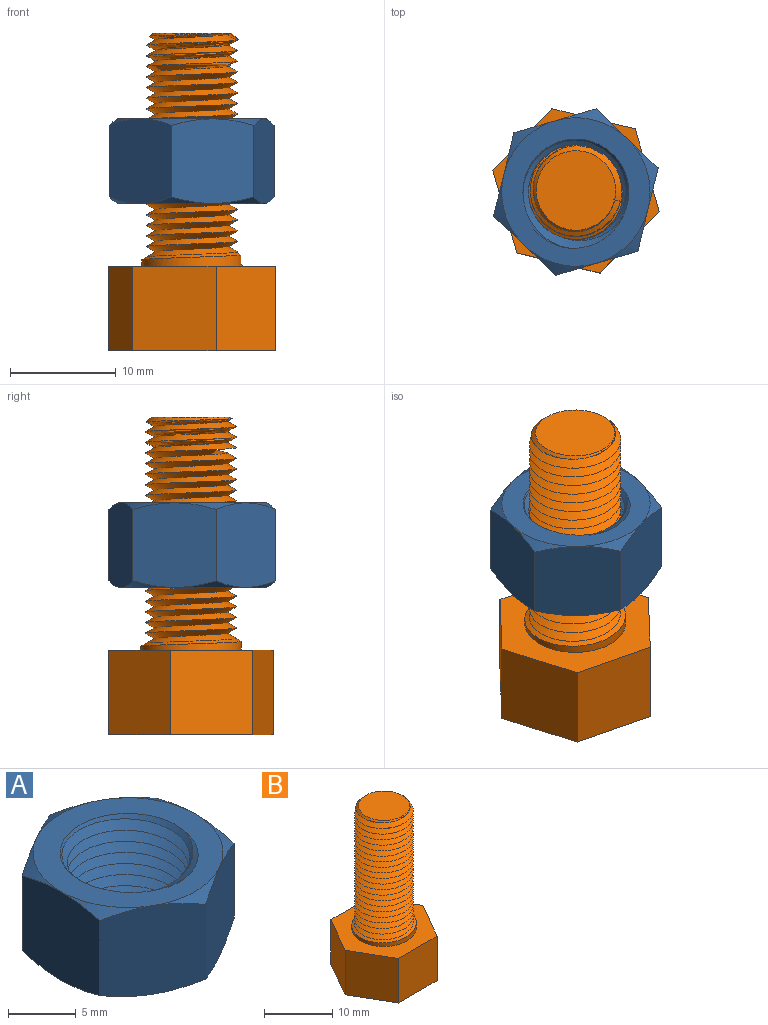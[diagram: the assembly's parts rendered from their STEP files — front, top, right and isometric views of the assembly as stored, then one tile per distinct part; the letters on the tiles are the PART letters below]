
ASSEMBLY  parts=2 mates=1
PART A: 24 faces, bbox 16.8x16.8x9.8 mm
  f0: plane 14.16x14.16mm, normal (0,0,1), area 73.3mm2, adj f4,f5,f7,f9,f11,f13,f21,f22
  f1: plane 14.16x14.16mm, normal (0,0,-1), area 73.3mm2, adj f2,f3,f6,f8,f10,f12,f20,f22
  f2: cone r=12.54mm half-angle=60deg, axis (0,0,1), area 4.8mm2, adj f1,f14,f19
  f3: cone r=12.54mm half-angle=60deg, axis (0,0,1), area 4.8mm2, adj f1,f14,f15
  f4: cone r=12.54mm half-angle=60deg, axis (0,0,-1), area 4.8mm2, adj f0,f14,f19
  f5: cone r=12.54mm half-angle=60deg, axis (0,0,-1), area 4.8mm2, adj f0,f14,f15
  f6: cone r=12.54mm half-angle=60deg, axis (0,0,1), area 4.8mm2, adj f1,f15,f16
  f7: cone r=12.54mm half-angle=60deg, axis (0,0,-1), area 4.8mm2, adj f0,f15,f16
  f8: cone r=12.54mm half-angle=60deg, axis (0,0,1), area 4.8mm2, adj f1,f16,f17
  f9: cone r=12.54mm half-angle=60deg, axis (0,0,-1), area 4.8mm2, adj f0,f16,f17
  f10: cone r=12.54mm half-angle=60deg, axis (0,0,1), area 4.8mm2, adj f1,f17,f18
  f11: cone r=12.54mm half-angle=60deg, axis (0,0,-1), area 4.8mm2, adj f0,f17,f18
  f12: cone r=12.54mm half-angle=60deg, axis (0,0,1), area 4.8mm2, adj f1,f18,f19
  f13: cone r=12.54mm half-angle=60deg, axis (0,0,-1), area 4.8mm2, adj f0,f18,f19
  f14: plane 8.76x8.67mm, normal (1,0,0), area 61.2mm2, adj f2,f3,f4,f5,f15,f19
  f15: plane 8.67x7.66mm, normal (0.5,-0.87,0), area 61.2mm2, adj f3,f5,f6,f7,f14,f16
  f16: plane 8.67x7.66mm, normal (-0.5,-0.87,0), area 61.2mm2, adj f6,f7,f8,f9,f15,f17
  f17: plane 8.76x8.67mm, normal (-1,0,0), area 61.2mm2, adj f8,f9,f10,f11,f16,f18
  f18: plane 8.67x7.66mm, normal (-0.5,0.87,0), area 61.2mm2, adj f10,f11,f12,f13,f17,f19
  f19: plane 8.67x7.66mm, normal (0.5,0.87,0), area 61.2mm2, adj f2,f4,f12,f13,f14,f18
  f20: cone r=5mm half-angle=45deg, axis (0,0,-1), area 6.9mm2, adj f1,f22,f23
  f21: cone r=4mm half-angle=45deg, axis (0,0,1), area 6.9mm2, adj f0,f22,f23
  f22: bspline ~12.33x10.68mm, area 236.9mm2, adj f0,f1,f20,f21,f23
  f23: bspline ~12.33x10.68mm, area 238.1mm2, adj f0,f1,f20,f21,f22
PART B: 17 faces, bbox 16.2x14x30.3 mm
  f0: plane 8x7mm, normal (-0.87,0.5,0), area 64.7mm2, adj f1,f5,f6,f7
  f1: plane 8x7mm, normal (-0.87,-0.5,0), area 64.7mm2, adj f0,f2,f6,f7
  f2: plane 8.08x8mm, normal (0,-1,0), area 64.7mm2, adj f1,f3,f6,f7
  f3: plane 8x7mm, normal (0.87,-0.5,0), area 64.7mm2, adj f2,f4,f6,f7
  f4: plane 8x7mm, normal (0.87,0.5,0), area 64.7mm2, adj f3,f5,f6,f7
  f5: plane 8.08x8mm, normal (0,1,0), area 64.7mm2, adj f0,f4,f6,f7
  f6: plane 16.17x14mm, normal (0,0,1), area 98.8mm2, adj f0,f1,f2,f3,f4,f5,f8
  f7: plane 16.17x14mm, normal (0,0,-1), area 169.7mm2, adj f0,f1,f2,f3,f4,f5
  f8: cylinder r=4.75mm len=9.5mm, axis (0,0,-1), area 16.5mm2, adj f6,f10,f14
  f9: plane 0.95x0.68mm, normal (0,-1,0), area 0.2mm2, adj f11,f12,f13,f16
  f10: plane 1.31x1.26mm, normal (0,1,0), area 0.9mm2, adj f8,f12,f13,f14
  f11: bspline ~4.12x2.6mm, area 0.2mm2, adj f9,f12,f16
  f12: bspline ~21.5x9.95mm, area 500mm2, adj f9,f10,f11,f13,f16
  f13: bspline ~21.5x9.95mm, area 508.6mm2, adj f9,f10,f12,f14
  f14: bspline ~10.97x9.5mm, area 14.6mm2, adj f8,f10,f13
  f15: plane 7.5x7.5mm, normal (0,0,1), area 44.2mm2, adj f16
  f16: cone r=3.75mm half-angle=45deg, axis (0,0,-1), area 11.4mm2, adj f9,f11,f12,f15
PLACE A rot(axis=(0,0,-1),13.7deg) t=(7.32,-10.88,1.65)mm
PLACE B rot(axis=(0,0,-1),13.7deg) t=(7.34,-10.75,-12.26)mm fixed
MATE slider B.f8 <-> A.f0  axis (0,0,1) through (7.34,-10.75,17.74)mm
